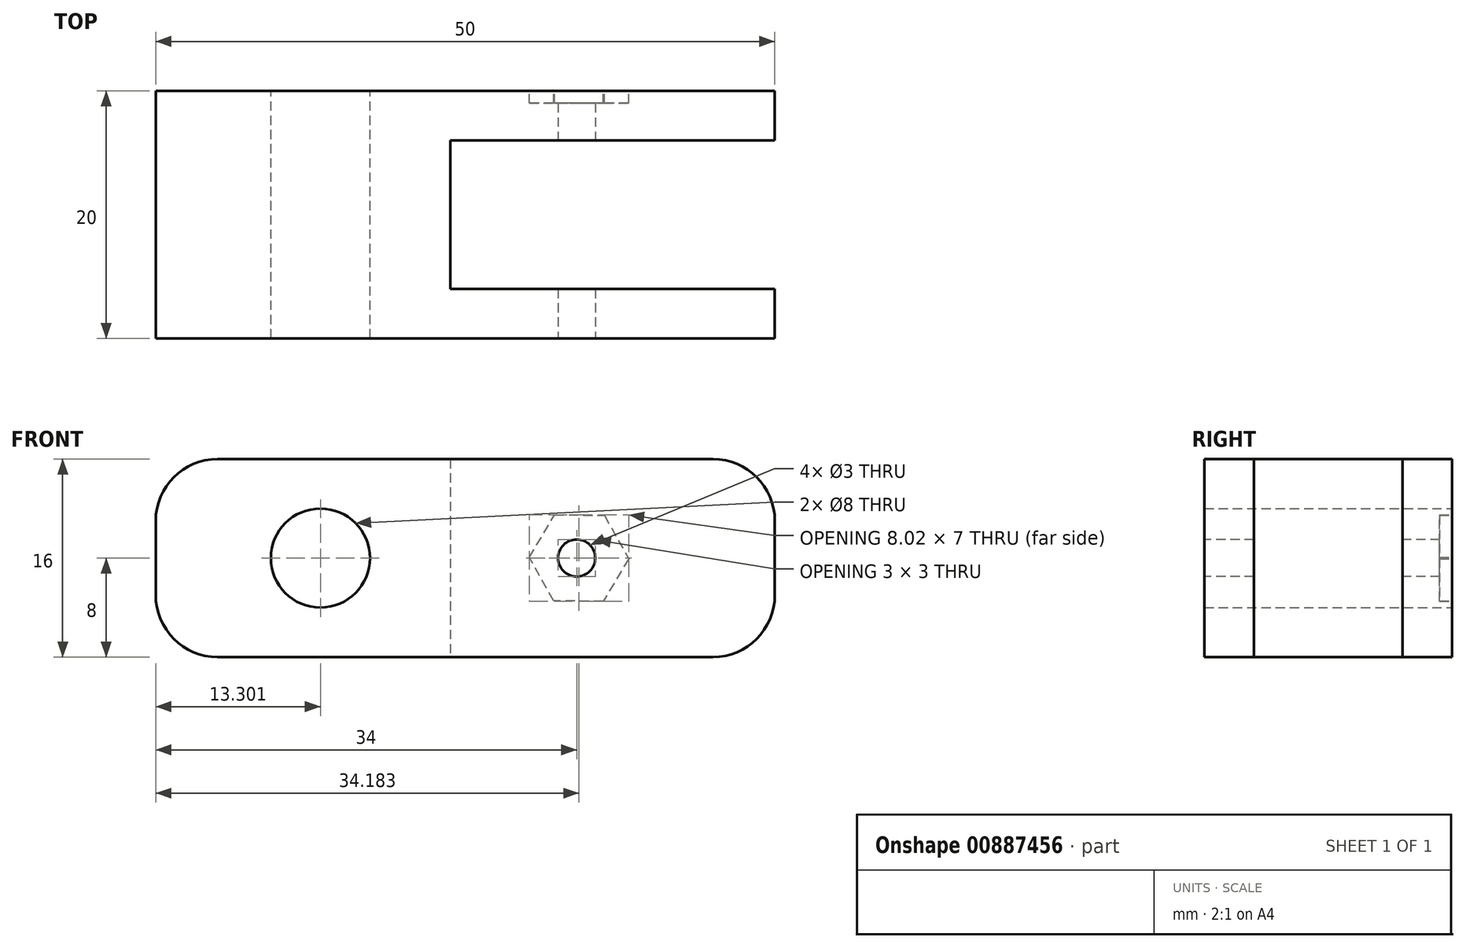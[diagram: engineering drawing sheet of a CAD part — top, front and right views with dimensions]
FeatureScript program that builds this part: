
annotation { "Feature Type Name" : "Feature", "Feature Type Description" : "" }
export const myFeature = defineFeature(function(context is Context, id is Id, definition is map)
    precondition{}
    {
        {
            var Q0;
            Q0=qCreatedBy(makeId("Front.planeOp"),FACE);
            var sketch = newSketch(context, id + "F0", { "sketchPlane" : qUnion([Q0])});
            skLineSegment(sketch, "E0.bottom", {"start": v(-25, -8) * mm, "end": v(25, -8) * mm});
            skLineSegment(sketch, "E0.top", {"start": v(-25, 8) * mm, "end": v(25, 8) * mm});
            skLineSegment(sketch, "E0.left", {"start": v(-25, -8) * mm, "end": v(-25, 8) * mm});
            skLineSegment(sketch, "E0.right", {"start": v(25, -8) * mm, "end": v(25, 8) * mm});
            skPoint(sketch, "E0.middle", {"position": v(0, 0) * mm});
            skSolve(sketch);
        }
        {
            var Q0;
            Q0=qCreatedBy(makeId("Front.planeOp"),FACE);
            var sketch = newSketch(context, id + "F1", { "sketchPlane" : qUnion([Q0])});
            skLineSegment(sketch, "E1", {"start": v(-25.54, 0) * mm, "end": v(-11.7, 0) * mm});
            skLineSegment(sketch, "E2", {"start": v(26.62, 0) * mm, "end": v(8.62, 0) * mm});
            skPoint(sketch, "E3", {"position": v(-11.7, 0) * mm});
            skPoint(sketch, "E4", {"position": v(8.62, 0) * mm});
            skSolve(sketch);
        }
        {
            var Q0;
            Q0=makeQuery(id+"F0.imprint","IMPRINT",FACE,{"disambiguationData":[TD([[makeQuery(id+"F0.imprint","IMPRINT",EDGE,{"derivedFrom":sQuery(id+"F0.wireOp",EDGE,"E0.bottom")}),1.0]])]});
            extrude(context, id + "F2", {"entities" : qUnion([Q0]), "depth" : 20 * mm, "offsetDistance" : 25 * mm});
        }
        {
            var Q0;
            Q0=sQuery(id+"F1.wireOp",VERTEX,"E3");
            var Q1;
            Q1=makeQuery(id+"F2.opExtrude","SWEPT_BODY",BODY,{"disambiguationData":[OSD([sQuery(id+"F0.wireOp",EDGE,"E0.bottom"),sQuery(id+"F0.wireOp",EDGE,"E0.top"),sQuery(id+"F0.wireOp",EDGE,"E0.left"),sQuery(id+"F0.wireOp",EDGE,"E0.right")])]});
            hole(context, id + "F3", {"style" : HoleStyle.SIMPLE, "endStyle" : HoleEndStyle.BLIND, "oppositeDirection" : true, "holeDiameter" : 8 * mm, "majorDiameter" : 5 * mm, "holeDepth" : 20 * mm, "isTappedThrough" : true, "tappedDepth" : 12 * mm, "tapClearance" : 3, "startFromSketch" : true, "locations" : qUnion([Q0]), "scope" : qUnion([Q1])});
        }
        {
            var Q0;
            Q0=makeQuery(id+"F2.opExtrude","CAP_FACE",FACE,{"disambiguationData":[OSD([sQuery(id+"F0.wireOp",EDGE,"E0.bottom"),sQuery(id+"F0.wireOp",EDGE,"E0.top"),sQuery(id+"F0.wireOp",EDGE,"E0.left"),sQuery(id+"F0.wireOp",EDGE,"E0.right")])],"isStart":false});
            var sketch = newSketch(context, id + "F4", { "sketchPlane" : qUnion([Q0])});
            skLineSegment(sketch, "E5", {"start": v(25, 0) * mm, "end": v(9, 0) * mm});
            skPoint(sketch, "E6", {"position": v(9, 0) * mm});
            skSolve(sketch);
        }
        {
            var Q0;
            Q0=sQuery(id+"F4.wireOp",VERTEX,"E6");
            var Q1;
            Q1=makeQuery(id+"F2.opExtrude","SWEPT_BODY",BODY,{"disambiguationData":[OSD([sQuery(id+"F0.wireOp",EDGE,"E0.bottom"),sQuery(id+"F0.wireOp",EDGE,"E0.top"),sQuery(id+"F0.wireOp",EDGE,"E0.left"),sQuery(id+"F0.wireOp",EDGE,"E0.right")])]});
            hole(context, id + "F5", {"style" : HoleStyle.SIMPLE, "endStyle" : HoleEndStyle.BLIND, "holeDiameter" : 3 * mm, "majorDiameter" : 5 * mm, "holeDepth" : 20 * mm, "isTappedThrough" : true, "tappedDepth" : 12 * mm, "tapClearance" : 3, "startFromSketch" : true, "locations" : qUnion([Q0]), "scope" : qUnion([Q1])});
        }
        {
            var Q0;
            Q0=makeQuery(id+"F2.opExtrude","SWEPT_FACE",FACE,{"disambiguationData":[OSD([sQuery(id+"F0.wireOp",EDGE,"E0.right")])]});
            var sketch = newSketch(context, id + "F6", { "sketchPlane" : qUnion([Q0])});
            skLineSegment(sketch, "E7", {"start": v(-20, 0) * mm, "end": v(-16, 0) * mm});
            skLineSegment(sketch, "E8", {"start": v(0, 0) * mm, "end": v(-4, 0) * mm});
            skLineSegment(sketch, "E9", {"start": v(-4, 8) * mm, "end": v(-4, -8) * mm});
            skLineSegment(sketch, "E10", {"start": v(-4, -8) * mm, "end": v(-16, -8) * mm});
            skLineSegment(sketch, "E11", {"start": v(-16, -8) * mm, "end": v(-16, 8) * mm});
            skLineSegment(sketch, "E12", {"start": v(-16, 8) * mm, "end": v(-4, 8) * mm});
            skSolve(sketch);
        }
        {
            var Q0;
            {var subQ2=sQuery(id+"F6.wireOp",EDGE,"E10");Q0=makeQuery(id+"F6.imprint","IMPRINT",FACE,{"disambiguationData":[TD([[makeQuery(id+"F6.imprint","IMPRINT",EDGE,{"derivedFrom":subQ2}),1.0]])]});}
            extrude(context, id + "F7", {"entities" : qUnion([Q0]), "operationType" : NewBodyOperationType.REMOVE, "oppositeDirection" : true, "depth" : 26.2 * mm, "offsetDistance" : 25 * mm});
        }
        {
            var Q0;
            {var subQ0=sQuery(id+"F0.wireOp",EDGE,"E0.right");var subQ1=sQuery(id+"F0.wireOp",EDGE,"E0.top");Q0=makeQuery(id+"F7.boolean.opBoolean","SPLIT",EDGE,{"disambiguationData":[TD([makeQuery(id+"F7.opExtrude","SWEPT_FACE",FACE,{"disambiguationData":[OSD([sQuery(id+"F6.wireOp",EDGE,"E11")])]})])],"derivedFrom":makeQuery(id+"F2.opExtrude","SWEPT_EDGE",EDGE,{"disambiguationData":[OSD([subQ1,subQ0])]})});}
            var Q1;
            {var subQ0=sQuery(id+"F0.wireOp",EDGE,"E0.right");var subQ1=sQuery(id+"F0.wireOp",EDGE,"E0.top");Q1=makeQuery(id+"F7.boolean.opBoolean","SPLIT",EDGE,{"disambiguationData":[TD([makeQuery(id+"F7.opExtrude","SWEPT_FACE",FACE,{"disambiguationData":[OSD([sQuery(id+"F6.wireOp",EDGE,"E9")])]})])],"derivedFrom":makeQuery(id+"F2.opExtrude","SWEPT_EDGE",EDGE,{"disambiguationData":[OSD([subQ1,subQ0])]})});}
            var Q2;
            {var subQ0=sQuery(id+"F0.wireOp",EDGE,"E0.bottom");var subQ1=sQuery(id+"F0.wireOp",EDGE,"E0.right");Q2=makeQuery(id+"F7.boolean.opBoolean","SPLIT",EDGE,{"disambiguationData":[TD([makeQuery(id+"F7.opExtrude","SWEPT_FACE",FACE,{"disambiguationData":[OSD([sQuery(id+"F6.wireOp",EDGE,"E11")])]})])],"derivedFrom":makeQuery(id+"F2.opExtrude","SWEPT_EDGE",EDGE,{"disambiguationData":[OSD([subQ0,subQ1])]})});}
            var Q3;
            {var subQ0=sQuery(id+"F0.wireOp",EDGE,"E0.bottom");var subQ1=sQuery(id+"F0.wireOp",EDGE,"E0.right");Q3=makeQuery(id+"F7.boolean.opBoolean","SPLIT",EDGE,{"disambiguationData":[TD([makeQuery(id+"F7.opExtrude","SWEPT_FACE",FACE,{"disambiguationData":[OSD([sQuery(id+"F6.wireOp",EDGE,"E9")])]})])],"derivedFrom":makeQuery(id+"F2.opExtrude","SWEPT_EDGE",EDGE,{"disambiguationData":[OSD([subQ0,subQ1])]})});}
            var Q4;
            Q4=makeQuery(id+"F2.opExtrude","SWEPT_EDGE",EDGE,{"disambiguationData":[OSD([sQuery(id+"F0.wireOp",EDGE,"E0.bottom"),sQuery(id+"F0.wireOp",EDGE,"E0.left")])]});
            var Q5;
            Q5=makeQuery(id+"F2.opExtrude","SWEPT_EDGE",EDGE,{"disambiguationData":[OSD([sQuery(id+"F0.wireOp",EDGE,"E0.top"),sQuery(id+"F0.wireOp",EDGE,"E0.left")])]});
            fillet(context, id + "F8", {"entities" : qUnion([Q0, Q1, Q2, Q3, Q4, Q5]), "radius" : 5 * mm, "tangentPropagation" : true, "allowEdgeOverflow" : false});
        }
        {
            var Q0;
            Q0=qCreatedBy(makeId("Front.planeOp"),FACE);
            var sketch = newSketch(context, id + "F9", { "sketchPlane" : qUnion([Q0])});
            skLineSegment(sketch, "E13", {"start": v(9.18, 0) * mm, "end": v(9.18, 3.14) * mm});
            skCircle(sketch, "E14.cCircle", {"center": v(9.18, 0) * mm, "radius": 3.47 * mm, "construction": true});
            skLineSegment(sketch, "E14.0", {"start": v(13.2, -0.05) * mm, "end": v(11.14, -3.5) * mm});
            skLineSegment(sketch, "E14.1", {"start": v(11.14, -3.5) * mm, "end": v(7.13, -3.45) * mm});
            skLineSegment(sketch, "E14.2", {"start": v(7.13, -3.45) * mm, "end": v(5.17, 0.05) * mm});
            skLineSegment(sketch, "E14.3", {"start": v(5.17, 0.05) * mm, "end": v(7.22, 3.5) * mm});
            skLineSegment(sketch, "E14.4", {"start": v(7.22, 3.5) * mm, "end": v(11.23, 3.45) * mm});
            skLineSegment(sketch, "E14.5", {"start": v(11.23, 3.45) * mm, "end": v(13.2, -0.05) * mm});
            skPoint(sketch, "E14.0.midPoint", {"position": v(12.17, -1.78) * mm});
            skSolve(sketch);
        }
        {
            var Q0;
            Q0=makeQuery(id+"F9.imprint","IMPRINT",FACE,{"disambiguationData":[TD([[makeQuery(id+"F9.imprint","IMPRINT",EDGE,{"derivedFrom":sQuery(id+"F9.wireOp",EDGE,"E14.0")}),-1.0]])]});
            extrude(context, id + "F10", {"entities" : qUnion([Q0]), "operationType" : NewBodyOperationType.REMOVE, "depth" : 1 * mm, "offsetDistance" : 25 * mm});
        }
    });
